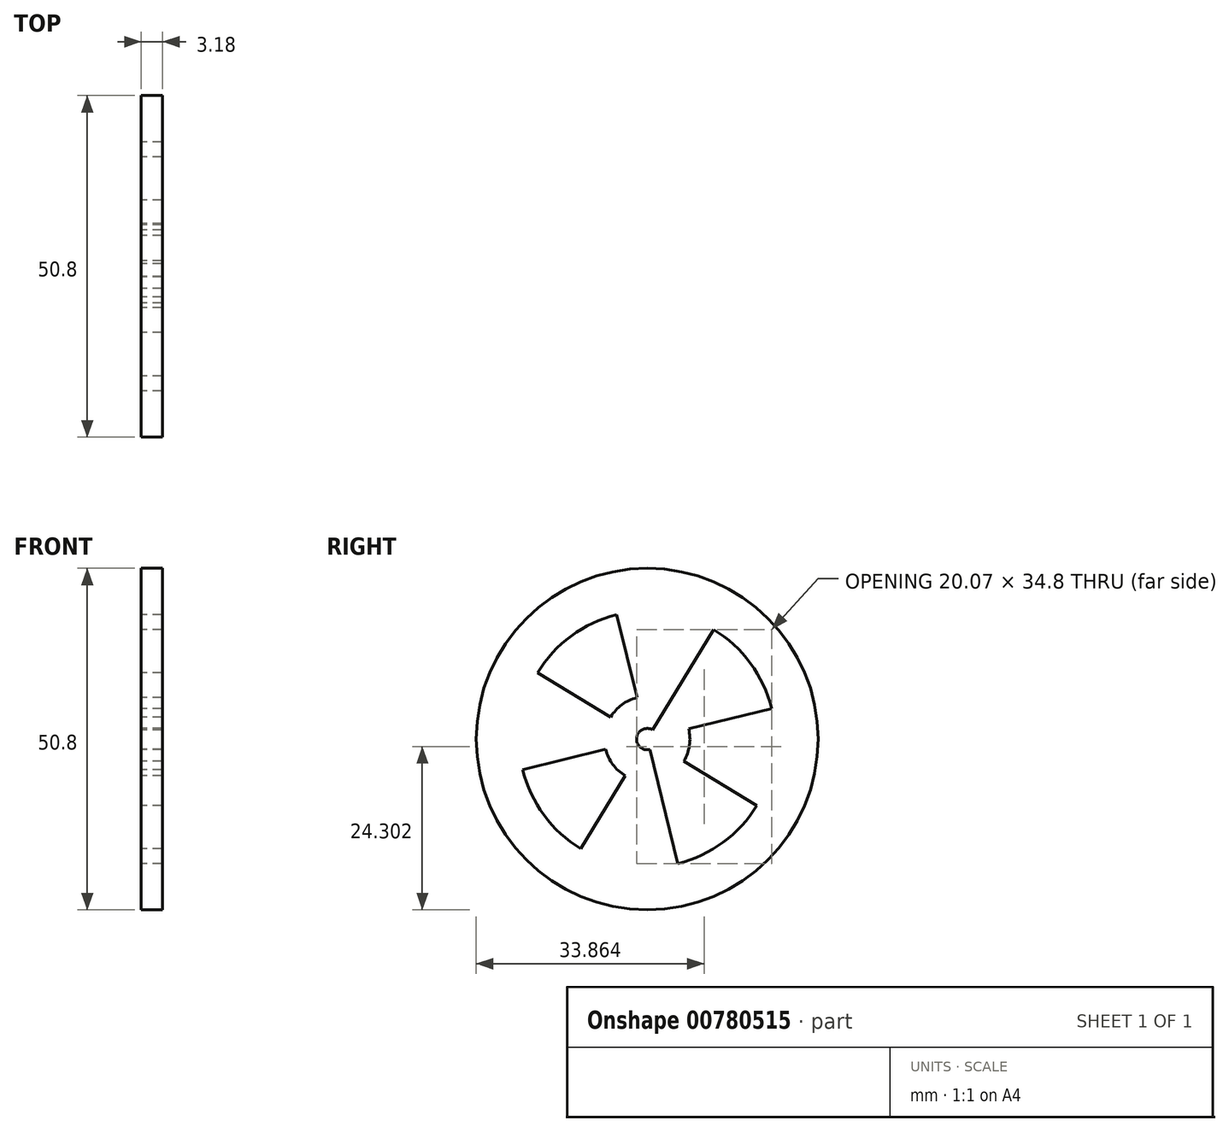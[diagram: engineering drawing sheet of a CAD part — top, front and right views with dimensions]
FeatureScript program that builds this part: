
annotation { "Feature Type Name" : "Feature", "Feature Type Description" : "" }
export const myFeature = defineFeature(function(context is Context, id is Id, definition is map)
    precondition{}
    {
        {
            var Q0;
            Q0=qCreatedBy(makeId("Right.planeOp"),FACE);
            var sketch = newSketch(context, id + "F0", { "sketchPlane" : qUnion([Q0])});
            skCircle(sketch, "E0", {"center": v(-41.8, 29.93) * mm, "radius": 6.35 * mm});
            skCircle(sketch, "E1", {"center": v(-41.8, 29.93) * mm, "radius": 25.4 * mm});
            skLineSegment(sketch, "E2", {"start": v(-36.38, 26.64) * mm, "end": v(-63.55, 43.07) * mm});
            skLineSegment(sketch, "E3", {"start": v(-41.65, 29.27) * mm, "end": v(-47.89, 54.6) * mm});
            skLineSegment(sketch, "E4.1.1", {"start": v(-38.52, 35.36) * mm, "end": v(-54.95, 8.2) * mm});
            skLineSegment(sketch, "E4.1.2", {"start": v(-41.15, 30.1) * mm, "end": v(-66.47, 23.85) * mm});
            skLineSegment(sketch, "E4.2.1", {"start": v(-47.24, 33.21) * mm, "end": v(-20.07, 16.79) * mm});
            skLineSegment(sketch, "E4.2.2", {"start": v(-41.97, 30.59) * mm, "end": v(-35.73, 5.27) * mm});
            skLineSegment(sketch, "E5.2.3.0", {"start": v(-45.1, 24.5) * mm, "end": v(-28.67, 51.67) * mm});
            skLineSegment(sketch, "E5.5.3.0", {"start": v(-42.47, 29.77) * mm, "end": v(-17.15, 36) * mm});
            skCircle(sketch, "E6.0", {"center": v(-41.8, 29.93) * mm, "radius": 19.05 * mm});
            skCircle(sketch, "E7.0", {"center": v(-41.8, 29.93) * mm, "radius": 1.59 * mm});
            skSolve(sketch);
        }
        {
            var Q0;
            {var subQ0=sQuery(id+"F0.wireOp",EDGE,"E1");var subQ1=sQuery(id+"F0.wireOp",EDGE,"E4.1.1");var subQ2=makeQuery(id+"F0.imprint","INTERSECT",VERTEX,{"derivedFrom":[subQ1,subQ0]});Q0=makeQuery(id+"F0.imprint","IMPRINT",FACE,{"disambiguationData":[TD([[makeQuery(id+"F0.imprint","IMPRINT",EDGE,{"disambiguationData":[TD([[subQ2,1.0]])],"derivedFrom":subQ1}),1.0]])]});}
            var Q1;
            {var subQ0=sQuery(id+"F0.wireOp",EDGE,"E0");var subQ5=sQuery(id+"F0.wireOp",EDGE,"E4.2.2");var subQ6=makeQuery(id+"F0.imprint","INTERSECT",VERTEX,{"derivedFrom":[subQ5,subQ0]});Q1=makeQuery(id+"F0.imprint","IMPRINT",FACE,{"disambiguationData":[TD([[makeQuery(id+"F0.imprint","IMPRINT",EDGE,{"disambiguationData":[TD([[subQ6,-1.0]])],"derivedFrom":subQ5}),-1.0]])]});}
            var Q2;
            {var subQ0=sQuery(id+"F0.wireOp",EDGE,"E1");var subQ1=sQuery(id+"F0.wireOp",EDGE,"E3");var subQ2=makeQuery(id+"F0.imprint","INTERSECT",VERTEX,{"derivedFrom":[subQ1,subQ0]});Q2=makeQuery(id+"F0.imprint","IMPRINT",FACE,{"disambiguationData":[TD([[makeQuery(id+"F0.imprint","IMPRINT",EDGE,{"disambiguationData":[TD([[subQ2,1.0]])],"derivedFrom":subQ1}),-1.0]])]});}
            var Q3;
            {var subQ0=sQuery(id+"F0.wireOp",EDGE,"E0");var subQ1=sQuery(id+"F0.wireOp",EDGE,"E3");var subQ2=makeQuery(id+"F0.imprint","INTERSECT",VERTEX,{"derivedFrom":[subQ1,subQ0]});Q3=makeQuery(id+"F0.imprint","IMPRINT",FACE,{"disambiguationData":[TD([[makeQuery(id+"F0.imprint","IMPRINT",EDGE,{"disambiguationData":[TD([[subQ2,-1.0]])],"derivedFrom":subQ1}),-1.0]])]});}
            var Q4;
            {var subQ0=sQuery(id+"F0.wireOp",EDGE,"E1");var subQ1=sQuery(id+"F0.wireOp",EDGE,"E4.2.1");var subQ2=makeQuery(id+"F0.imprint","INTERSECT",VERTEX,{"derivedFrom":[subQ1,subQ0]});Q4=makeQuery(id+"F0.imprint","IMPRINT",FACE,{"disambiguationData":[TD([[makeQuery(id+"F0.imprint","IMPRINT",EDGE,{"disambiguationData":[TD([[subQ2,1.0]])],"derivedFrom":subQ1}),1.0]])]});}
            var Q5;
            {var subQ0=sQuery(id+"F0.wireOp",EDGE,"E0");var subQ1=sQuery(id+"F0.wireOp",EDGE,"E4.2.1");var subQ2=makeQuery(id+"F0.imprint","INTERSECT",VERTEX,{"derivedFrom":[subQ1,subQ0]});Q5=makeQuery(id+"F0.imprint","IMPRINT",FACE,{"disambiguationData":[TD([[makeQuery(id+"F0.imprint","IMPRINT",EDGE,{"disambiguationData":[TD([[subQ2,-1.0]])],"derivedFrom":subQ1}),1.0]])]});}
            var Q6;
            {var subQ0=sQuery(id+"F0.wireOp",EDGE,"E1");var subQ1=sQuery(id+"F0.wireOp",EDGE,"E2");var subQ2=makeQuery(id+"F0.imprint","INTERSECT",VERTEX,{"derivedFrom":[subQ1,subQ0]});Q6=makeQuery(id+"F0.imprint","IMPRINT",FACE,{"disambiguationData":[TD([[makeQuery(id+"F0.imprint","IMPRINT",EDGE,{"disambiguationData":[TD([[subQ2,1.0]])],"derivedFrom":subQ1}),1.0]])]});}
            var Q7;
            {var subQ0=sQuery(id+"F0.wireOp",EDGE,"E1");var subQ1=sQuery(id+"F0.wireOp",EDGE,"E2");var subQ2=makeQuery(id+"F0.imprint","INTERSECT",VERTEX,{"derivedFrom":[subQ1,subQ0]});Q7=makeQuery(id+"F0.imprint","IMPRINT",FACE,{"disambiguationData":[TD([[makeQuery(id+"F0.imprint","IMPRINT",EDGE,{"disambiguationData":[TD([[subQ2,1.0]])],"derivedFrom":subQ1}),-1.0]])]});}
            var Q8;
            {var subQ0=sQuery(id+"F0.wireOp",EDGE,"E1");var subQ1=sQuery(id+"F0.wireOp",EDGE,"E5.2.3.0");var subQ2=makeQuery(id+"F0.imprint","INTERSECT",VERTEX,{"derivedFrom":[subQ1,subQ0]});Q8=makeQuery(id+"F0.imprint","IMPRINT",FACE,{"disambiguationData":[TD([[makeQuery(id+"F0.imprint","IMPRINT",EDGE,{"disambiguationData":[TD([[subQ2,1.0]])],"derivedFrom":subQ1}),-1.0]])]});}
            var Q9;
            {var subQ0=sQuery(id+"F0.wireOp",EDGE,"E1");var subQ1=sQuery(id+"F0.wireOp",EDGE,"E4.2.1");var subQ2=makeQuery(id+"F0.imprint","INTERSECT",VERTEX,{"derivedFrom":[subQ1,subQ0]});Q9=makeQuery(id+"F0.imprint","IMPRINT",FACE,{"disambiguationData":[TD([[makeQuery(id+"F0.imprint","IMPRINT",EDGE,{"disambiguationData":[TD([[subQ2,1.0]])],"derivedFrom":subQ1}),-1.0]])]});}
            var Q10;
            {var subQ0=sQuery(id+"F0.wireOp",EDGE,"E1");var subQ1=sQuery(id+"F0.wireOp",EDGE,"E4.1.1");var subQ2=makeQuery(id+"F0.imprint","INTERSECT",VERTEX,{"derivedFrom":[subQ1,subQ0]});Q10=makeQuery(id+"F0.imprint","IMPRINT",FACE,{"disambiguationData":[TD([[makeQuery(id+"F0.imprint","IMPRINT",EDGE,{"disambiguationData":[TD([[subQ2,1.0]])],"derivedFrom":subQ1}),-1.0]])]});}
            var Q11;
            {var subQ0=sQuery(id+"F0.wireOp",EDGE,"E0");var subQ5=sQuery(id+"F0.wireOp",EDGE,"E4.1.2");var subQ6=makeQuery(id+"F0.imprint","INTERSECT",VERTEX,{"derivedFrom":[subQ5,subQ0]});Q11=makeQuery(id+"F0.imprint","IMPRINT",FACE,{"disambiguationData":[TD([[makeQuery(id+"F0.imprint","IMPRINT",EDGE,{"disambiguationData":[TD([[subQ6,-1.0]])],"derivedFrom":subQ5}),-1.0]])]});}
            var Q12;
            {var subQ0=sQuery(id+"F0.wireOp",EDGE,"E7.0");var subQ1=sQuery(id+"F0.wireOp",EDGE,"E4.1.2");var subQ2=makeQuery(id+"F0.imprint","INTERSECT",VERTEX,{"derivedFrom":[subQ1,subQ0]});Q12=makeQuery(id+"F0.imprint","IMPRINT",FACE,{"disambiguationData":[TD([[makeQuery(id+"F0.imprint","IMPRINT",EDGE,{"disambiguationData":[TD([[subQ2,-1.0]])],"derivedFrom":subQ1}),-1.0]])]});}
            var Q13;
            {var subQ0=sQuery(id+"F0.wireOp",EDGE,"E7.0");var subQ1=sQuery(id+"F0.wireOp",EDGE,"E3");var subQ2=makeQuery(id+"F0.imprint","INTERSECT",VERTEX,{"derivedFrom":[subQ1,subQ0]});Q13=makeQuery(id+"F0.imprint","IMPRINT",FACE,{"disambiguationData":[TD([[makeQuery(id+"F0.imprint","IMPRINT",EDGE,{"disambiguationData":[TD([[subQ2,-1.0]])],"derivedFrom":subQ1}),-1.0]])]});}
            var Q14;
            {var subQ0=sQuery(id+"F0.wireOp",EDGE,"E7.0");var subQ1=sQuery(id+"F0.wireOp",EDGE,"E4.2.1");var subQ2=makeQuery(id+"F0.imprint","INTERSECT",VERTEX,{"disambiguationData":[OD(1.0)],"derivedFrom":[subQ1,subQ0]});Q14=makeQuery(id+"F0.imprint","IMPRINT",FACE,{"disambiguationData":[TD([[makeQuery(id+"F0.imprint","IMPRINT",EDGE,{"disambiguationData":[TD([[subQ2,-1.0]])],"derivedFrom":subQ1}),1.0]])]});}
            var Q15;
            {var subQ0=sQuery(id+"F0.wireOp",EDGE,"E7.0");var subQ1=sQuery(id+"F0.wireOp",EDGE,"E3");var subQ2=makeQuery(id+"F0.imprint","INTERSECT",VERTEX,{"derivedFrom":[subQ1,subQ0]});Q15=makeQuery(id+"F0.imprint","IMPRINT",FACE,{"disambiguationData":[TD([[makeQuery(id+"F0.imprint","IMPRINT",EDGE,{"disambiguationData":[TD([[subQ2,-1.0]])],"derivedFrom":subQ1}),1.0]])]});}
            var Q16;
            {var subQ0=sQuery(id+"F0.wireOp",EDGE,"E7.0");var subQ1=sQuery(id+"F0.wireOp",EDGE,"E4.1.2");var subQ2=makeQuery(id+"F0.imprint","INTERSECT",VERTEX,{"derivedFrom":[subQ1,subQ0]});Q16=makeQuery(id+"F0.imprint","IMPRINT",FACE,{"disambiguationData":[TD([[makeQuery(id+"F0.imprint","IMPRINT",EDGE,{"disambiguationData":[TD([[subQ2,-1.0]])],"derivedFrom":subQ1}),1.0]])]});}
            var Q17;
            {var subQ0=sQuery(id+"F0.wireOp",EDGE,"E7.0");var subQ1=sQuery(id+"F0.wireOp",EDGE,"E4.2.1");var subQ2=makeQuery(id+"F0.imprint","INTERSECT",VERTEX,{"disambiguationData":[OD(1.0)],"derivedFrom":[subQ1,subQ0]});Q17=makeQuery(id+"F0.imprint","IMPRINT",FACE,{"disambiguationData":[TD([[makeQuery(id+"F0.imprint","IMPRINT",EDGE,{"disambiguationData":[TD([[subQ2,-1.0]])],"derivedFrom":subQ1}),-1.0]])]});}
            var Q18;
            {var subQ0=sQuery(id+"F0.wireOp",EDGE,"E7.0");var subQ1=sQuery(id+"F0.wireOp",EDGE,"E5.2.3.0");var subQ2=makeQuery(id+"F0.imprint","INTERSECT",VERTEX,{"disambiguationData":[OD(1.0)],"derivedFrom":[subQ1,subQ0]});Q18=makeQuery(id+"F0.imprint","IMPRINT",FACE,{"disambiguationData":[TD([[makeQuery(id+"F0.imprint","IMPRINT",EDGE,{"disambiguationData":[TD([[subQ2,-1.0]])],"derivedFrom":subQ1}),-1.0]])]});}
            var Q19;
            {var subQ0=sQuery(id+"F0.wireOp",EDGE,"E7.0");var subQ1=sQuery(id+"F0.wireOp",EDGE,"E4.2.2");var subQ2=makeQuery(id+"F0.imprint","INTERSECT",VERTEX,{"derivedFrom":[subQ1,subQ0]});Q19=makeQuery(id+"F0.imprint","IMPRINT",FACE,{"disambiguationData":[TD([[makeQuery(id+"F0.imprint","IMPRINT",EDGE,{"disambiguationData":[TD([[subQ2,-1.0]])],"derivedFrom":subQ1}),-1.0]])]});}
            extrude(context, id + "F1", {"entities" : qUnion([Q0, Q1, Q2, Q3, Q4, Q5, Q6, Q7, Q8, Q9, Q10, Q11, Q12, Q13, Q14, Q15, Q16, Q17, Q18, Q19]), "depth" : 3.17 * mm, "offsetDistance" : 25.4 * mm});
        }
    });
